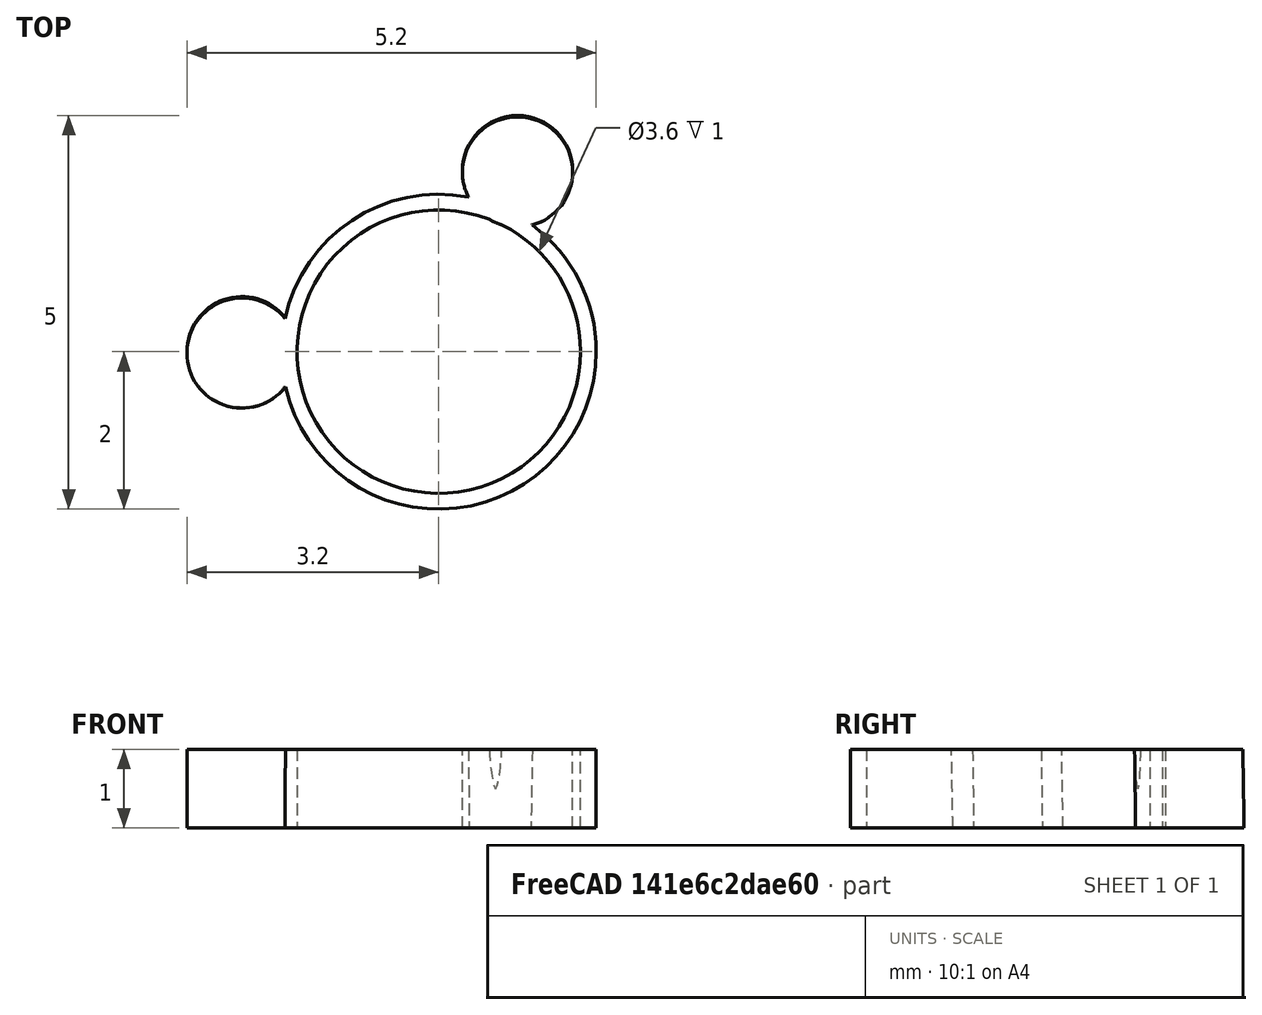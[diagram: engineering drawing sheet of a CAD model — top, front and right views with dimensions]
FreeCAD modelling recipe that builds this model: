
FCSTD DOCUMENT  (FreeCAD 1.0R38806 (Git))
Label: anillo
License: All rights reserved
LicenseURL: https://en.wikipedia.org/wiki/All_rights_reserved
objects: Part::Cylinder×4, Part::Cut×1, Part::Fuse×1, Part::MultiFuse×1
note: 7 computed .brp shape members not serialized (recipe doc carries the construction recipe); baked Part::Feature solids carry a one-line shape summary decoded from their .brp

FEATURE [Part::Cylinder] Cylinder  label="Cilindro"
  Angle = 360
  AttacherType = Attacher::AttachEngine3D
  FirstAngle = 0
  Height = 1
  Radius = 2
  SecondAngle = 0
FEATURE [Part::Cylinder] Cylinder001  label="Cilindro001"
  Angle = 360
  AttacherType = Attacher::AttachEngine3D
  FirstAngle = 0
  Height = 1
  Radius = 1.8
  SecondAngle = 0
FEATURE [Part::Cut] Cut
  Base = -> Cylinder
  Refine = true
  Tool = -> Cylinder001
FEATURE [Part::Cylinder] Cylinder002  label="Cilindro002"
  Angle = 360
  AttacherType = Attacher::AttachEngine3D
  FirstAngle = 0
  Height = 1
  Placement = pos=(-2.5,0,0) rot=(0,-0.1,1;0rad)
  Radius = 0.7
  SecondAngle = -1
FEATURE [Part::Cylinder] Cylinder003  label="Cilindro003"
  Angle = 360
  AttacherType = Attacher::AttachEngine3D
  FirstAngle = 0
  Height = 1
  Placement = pos=(1,2.3,0) rot=(0,-0.1,1;0rad)
  Radius = 0.7
  SecondAngle = -1
FEATURE [Part::Fuse] Fusion
  Base = -> Cut
  Refine = true
  Tool = -> Cylinder002
FEATURE [Part::MultiFuse] Fusion001
  Refine = true
  Shapes = -> [Cut,Cylinder002,Cylinder003,Fusion]
